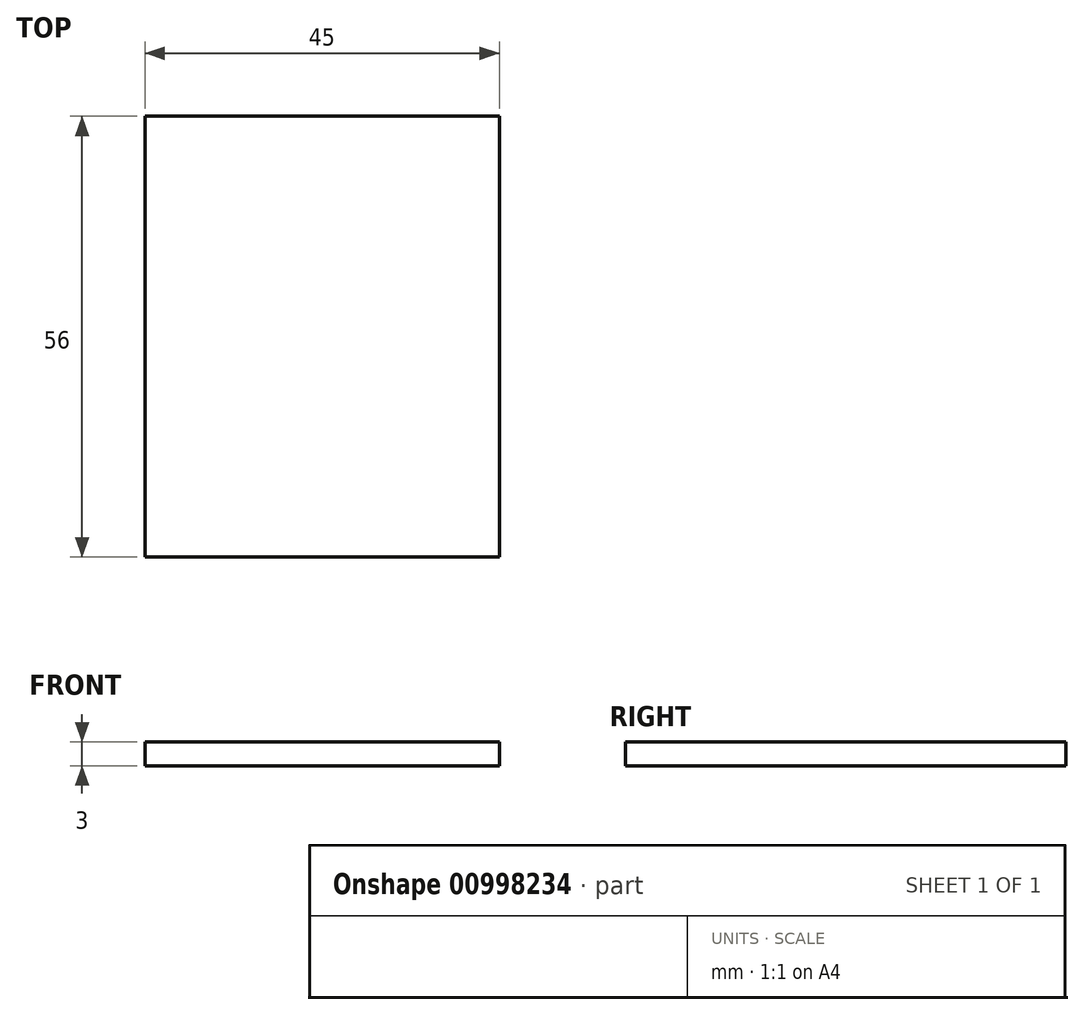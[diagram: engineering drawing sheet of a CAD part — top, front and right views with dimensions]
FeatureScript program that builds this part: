
annotation { "Feature Type Name" : "Feature", "Feature Type Description" : "" }
export const myFeature = defineFeature(function(context is Context, id is Id, definition is map)
    precondition{}
    {
        {
            var Q0;
            Q0=qCreatedBy(makeId("Top.planeOp"),FACE);
            var sketch = newSketch(context, id + "F0", { "sketchPlane" : qUnion([Q0])});
            skLineSegment(sketch, "E0.bottom", {"start": v(0, 0) * mm, "end": v(45, 0) * mm});
            skLineSegment(sketch, "E0.top", {"start": v(0, 56) * mm, "end": v(45, 56) * mm});
            skLineSegment(sketch, "E0.left", {"start": v(0, 0) * mm, "end": v(0, 56) * mm});
            skLineSegment(sketch, "E0.right", {"start": v(45, 0) * mm, "end": v(45, 56) * mm});
            skSolve(sketch);
        }
        {
            var Q0;
            Q0 = qSketchRegion(id + "F0", true);
            extrude(context, id + "F1", {"entities" : qUnion([Q0]), "depth" : 3 * mm, "offsetDistance" : 25 * mm});
        }
    });
